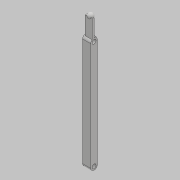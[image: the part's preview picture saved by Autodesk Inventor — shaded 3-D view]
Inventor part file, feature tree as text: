
AUTODESK INVENTOR PART (.ipt)
format: ipt  version: 2018 (Build 220112000, 112)  size: 176,128 bytes
history: native  units: mm
features: sketch x9, extrude x7, other x5, plane x5, fillet x2, hole x2, projected_geometry x2, mirror x1
ambient origin geometry x8: Origin, YZ Plane, XZ Plane, XY Plane, X Axis, Y Axis, Z Axis, Center Point
bodies: Body1 (feature_tree)
feature tree (33):
  other  "實體1"
  extrude  "擠出1"  Depth=5.0mm
  fillet  "圓角1"  Radius=85.0mm
  hole  "孔1"  [1 undecoded]
  fillet  "圓角2"  Radius=2.5mm
  hole  "孔2"  [1 undecoded]
  extrude  "擠出2"  Depth=2.5mm
  plane  "工作平面1"
  extrude  "擠出3"  Depth=10.0mm
  other  "迴轉1"
  other  "工作軸線1"
  plane  "工作平面3"
  mirror  "鏡射1"
  extrude  "擠出4"  Depth=3.0mm
  extrude  "擠出5"  Depth=16.0mm
  extrude  "擠出6"  Depth=5.0mm TaperAngle=0.0deg
  extrude  "擠出7"  Depth=6.0mm TaperAngle=0.0deg
  plane  "工作平面5"
  other  "迴轉3"
  sketch  "草圖1"
  sketch  "草圖2"
  projected_geometry  "投影迴路1"
  sketch  "草圖3"
  sketch  "草圖4"
  other  "工作軸線2"
  plane  "工作平面2"
  plane  "工作平面4"
  sketch  "草圖5"
  projected_geometry  "投影迴路2"
  sketch  "草圖6"
  sketch  "草圖7"
  sketch  "草圖8"
  sketch  "草圖10"
note: 2 required parameter values undecoded (feature->parameter linkage not recoverable at this tier; creation-order binding heuristic only, values carry confidence <= 0.55)
